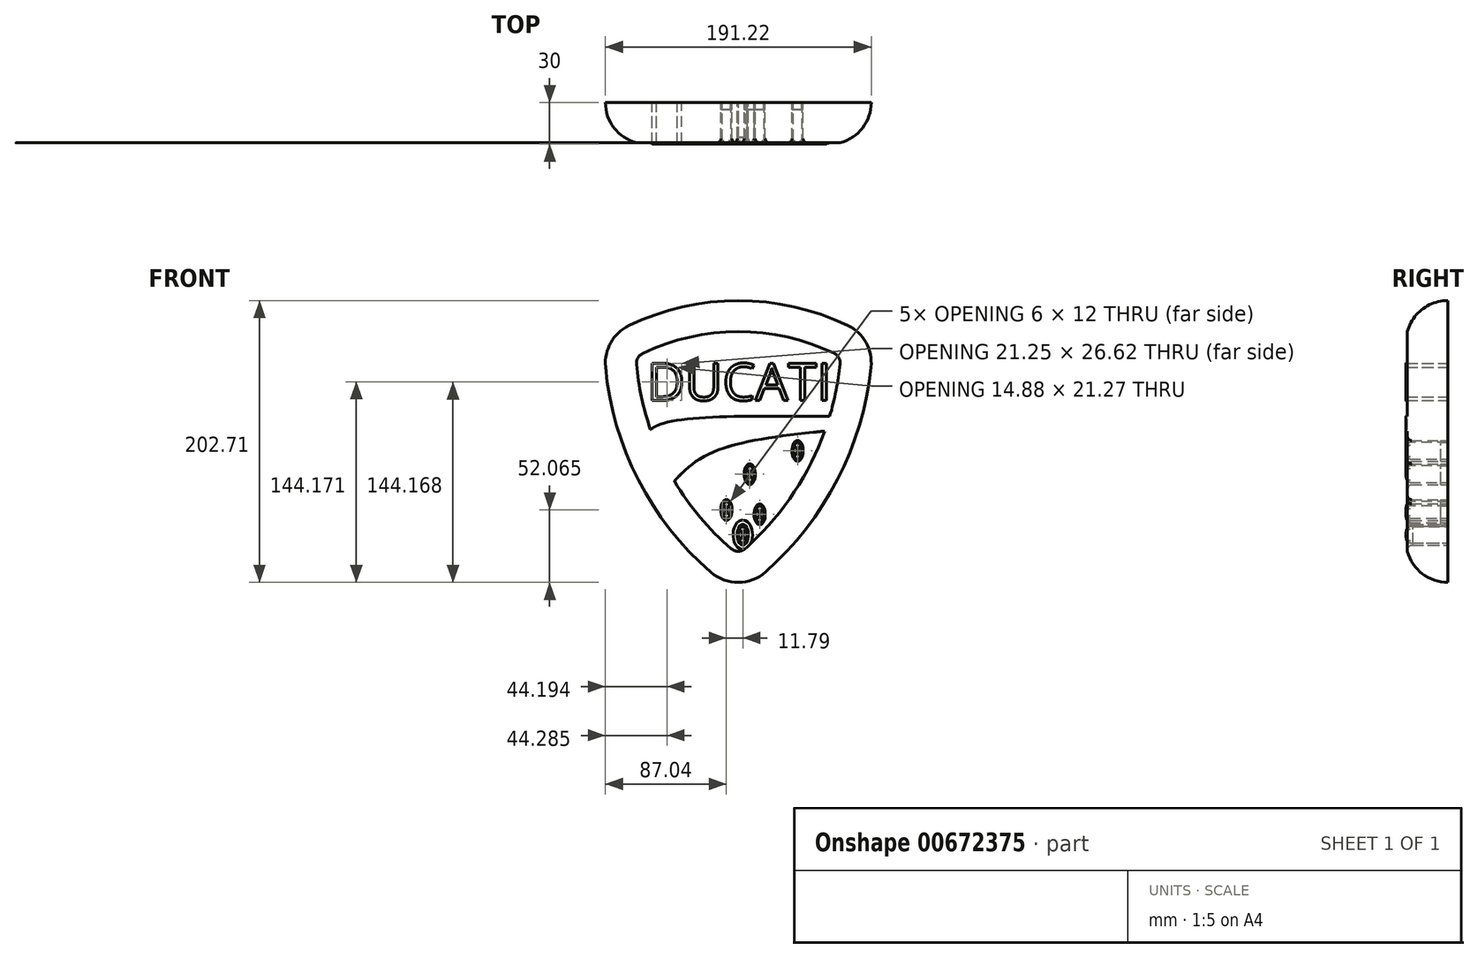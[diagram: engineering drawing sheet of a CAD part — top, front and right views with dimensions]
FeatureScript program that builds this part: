
annotation { "Feature Type Name" : "Feature", "Feature Type Description" : "" }
export const myFeature = defineFeature(function(context is Context, id is Id, definition is map)
    precondition{}
    {
        {
            var Q0;
            Q0=qCreatedBy(makeId("Front.planeOp"),FACE);
            var sketch = newSketch(context, id + "F0", { "sketchPlane" : qUnion([Q0])});
            skPoint(sketch, "E0.middle", {"position": v(0, 0) * mm});
            skArc(sketch, "E1", {"start": v(75.34, 85.7) * mm, "mid": v(-3.27, 103.48) * mm, "end": v(-81.84, 85.51) * mm});
            skArc(sketch, "E2", {"start": v(16.55, -91.67) * mm, "mid": v(68.15, -25.17) * mm, "end": v(92.22, 55.48) * mm});
            skArc(sketch, "E3", {"start": v(-98.71, 55.8) * mm, "mid": v(-75.23, -25.43) * mm, "end": v(-22.98, -91.93) * mm});
            skArc(sketch, "E4.filletArc", {"start": v(92.22, 55.48) * mm, "mid": v(88.57, 73.27) * mm, "end": v(75.34, 85.7) * mm});
            skArc(sketch, "E5.filletArc", {"start": v(-81.84, 85.51) * mm, "mid": v(-94.92, 73.3) * mm, "end": v(-98.71, 55.8) * mm});
            skArc(sketch, "E6.filletArc", {"start": v(-22.98, -91.93) * mm, "mid": v(-3.17, -99.23) * mm, "end": v(16.55, -91.67) * mm});
            skPoint(sketch, "E7", {"position": v(-75.34, 72) * mm});
            skPoint(sketch, "E8", {"position": v(-83.77, 57.14) * mm});
            skPoint(sketch, "E9", {"position": v(-3.06, 88.48) * mm});
            skPoint(sketch, "E10", {"position": v(68.86, 72.16) * mm});
            skPoint(sketch, "E11", {"position": v(77.3, 57.06) * mm});
            skPoint(sketch, "E12", {"position": v(6.6, -80.45) * mm});
            skPoint(sketch, "E13", {"position": v(-13.17, -80.58) * mm});
            skPoint(sketch, "E14", {"position": v(-75.23, -25.43) * mm});
            skPoint(sketch, "E15", {"position": v(68.15, -25.17) * mm});
            skPoint(sketch, "E16", {"position": v(55.35, -17.35) * mm});
            skArc(sketch, "E17", {"start": v(68.86, 72.16) * mm, "mid": v(-3.26, 88.48) * mm, "end": v(-75.34, 72) * mm});
            skArc(sketch, "E18", {"start": v(6.6, -80.45) * mm, "mid": v(42.72, -38.97) * mm, "end": v(67.05, 10.37) * mm});
            skArc(sketch, "E19", {"start": v(-50.14, -38.7) * mm, "mid": v(-33.09, -60.9) * mm, "end": v(-13.17, -80.58) * mm});
            skArc(sketch, "E20", {"start": v(-75.34, 72) * mm, "mid": v(-81.7, 65.79) * mm, "end": v(-83.77, 57.14) * mm});
            skArc(sketch, "E21", {"start": v(77.3, 57.06) * mm, "mid": v(75.3, 65.85) * mm, "end": v(68.86, 72.16) * mm});
            skArc(sketch, "E22", {"start": v(-13.17, -80.58) * mm, "mid": v(-3.27, -83.93) * mm, "end": v(6.6, -80.45) * mm});
            skPoint(sketch, "E23", {"position": v(-71, 62.98) * mm});
            skPoint(sketch, "E24", {"position": v(64.55, 63.14) * mm});
            skLineSegment(sketch, "E25", {"start": v(-68.8, 31.48) * mm, "end": v(62.42, 31.63) * mm, "construction": true});
            skText(sketch, "E26", { "text": "DUCATI", "fontName": "OpenSans-Regular.ttf"});
            skPoint(sketch, "E27", {"position": v(70.13, 20.17) * mm});
            skPoint(sketch, "E28", {"position": v(-71.8, 3.86) * mm});
            skPoint(sketch, "E29", {"position": v(65.47, 5.91) * mm});
            skFitSpline(sketch, "E30", {"points": [v(-71.8, 3.86) * mm, v(-60.64, 13.97) * mm, v(70.13, 20.17) * mm], "startDerivative": vector(27.5, 43.67) * mm, "endDerivative": vector(224.9, 0.03) * mm});
            skFitSpline(sketch, "E31", {"points": [v(-54.27, -32.24) * mm, v(-24.16, -6.71) * mm, v(67.05, 10.37) * mm], "startDerivative": vector(61.57, 71.85) * mm, "endDerivative": vector(173.13, 17.23) * mm});
            skArc(sketch, "E32.filletArc", {"start": v(-49.27, -26.5) * mm, "mid": v(-51.8, -32.45) * mm, "end": v(-50.14, -38.7) * mm});
            skArc(sketch, "E33", {"start": v(-83.77, 57.14) * mm, "mid": v(-79.56, 30.1) * mm, "end": v(-71.8, 3.86) * mm});
            skEllipse(sketch, "E34", {"center": v(-11.79, -47.16) * mm, "majorRadius": 7.5 * mm, "minorRadius": 4 * mm, "majorAxis": v(0, -1)});
            skEllipse(sketch, "E35", {"center": v(4.98, -21.44) * mm, "majorRadius": 7.5 * mm, "minorRadius": 4 * mm, "majorAxis": v(0, -1)});
            skEllipse(sketch, "E36", {"center": v(12.14, -50.3) * mm, "majorRadius": 7.5 * mm, "minorRadius": 4 * mm, "majorAxis": v(0, -1)});
            skEllipse(sketch, "E37", {"center": v(39.41, -4.67) * mm, "majorRadius": 7.5 * mm, "minorRadius": 4 * mm, "majorAxis": v(0, -1)});
            skPoint(sketch, "E38.start.orphan", {"position": v(-3.07, 103.48) * mm});
            skArc(sketch, "E39.trimOffspring", {"start": v(70.13, 20.17) * mm, "mid": v(74.53, 38.46) * mm, "end": v(77.3, 57.06) * mm});
            skEllipse(sketch, "E40", {"center": v(0, -65.02) * mm, "majorRadius": 7.5 * mm, "minorRadius": 4 * mm, "majorAxis": v(0, -1)});
            skEllipse(sketch, "E41", {"center": v(4.98, -21.44) * mm, "majorRadius": 6 * mm, "minorRadius": 3 * mm, "majorAxis": v(0, -1)});
            skEllipse(sketch, "E42", {"center": v(-11.79, -47.16) * mm, "majorRadius": 6 * mm, "minorRadius": 3 * mm, "majorAxis": v(0, -1)});
            skEllipse(sketch, "E43", {"center": v(0, -65.02) * mm, "majorRadius": 6 * mm, "minorRadius": 3 * mm, "majorAxis": v(0, -1)});
            skEllipse(sketch, "E44", {"center": v(12.14, -50.3) * mm, "majorRadius": 6 * mm, "minorRadius": 3 * mm, "majorAxis": v(0, -1)});
            skEllipse(sketch, "E45", {"center": v(39.41, -4.67) * mm, "majorRadius": 6 * mm, "minorRadius": 3 * mm, "majorAxis": v(0, -1)});
            const initialGuessF0  = {"E26": [-0.06883, 0.03163, 1, 0, 0.02685]};
            skSetInitialGuess(sketch, initialGuessF0);
            skSolve(sketch);
        }
        {
            var Q0;
            Q0=makeQuery(id+"F0.imprint","IMPRINT",FACE,{"disambiguationData":[TD([[makeQuery(id+"F0.imprint","IMPRINT",EDGE,{"derivedFrom":sQuery(id+"F0.wireOp",EDGE,"E1")}),1.0]])]});
            extrude(context, id + "F1", {"entities" : qUnion([Q0]), "depth" : 30 * mm, "offsetDistance" : 25 * mm});
        }
        {
            var Q0;
            Q0=makeQuery(id+"F0.imprint","IMPRINT",FACE,{"disambiguationData":[TD([[makeQuery(id+"F0.imprint","IMPRINT",EDGE,{"derivedFrom":sQuery(id+"F0.wireOp",EDGE,"E17")}),1.0]])]});
            extrude(context, id + "F2", {"entities" : qUnion([Q0]), "operationType" : NewBodyOperationType.ADD, "depth" : 29 * mm, "offsetDistance" : 25 * mm});
        }
        {
            var Q0;
            Q0=makeQuery(id+"F0.imprint","IMPRINT",FACE,{"disambiguationData":[TD([[makeQuery(id+"F0.imprint","IMPRINT",EDGE,{"derivedFrom":sQuery(id+"F0.wireOp",EDGE,"E26.sketch_text.stroke-7")}),1.0]])]});
            extrude(context, id + "F3", {"entities" : qUnion([Q0]), "depth" : 29 * mm, "offsetDistance" : 25 * mm});
        }
        {
            var Q0;
            Q0=makeQuery(id+"F0.imprint","IMPRINT",FACE,{"disambiguationData":[TD([[makeQuery(id+"F0.imprint","IMPRINT",EDGE,{"derivedFrom":sQuery(id+"F0.wireOp",EDGE,"E18")}),1.0]])]});
            extrude(context, id + "F4", {"entities" : qUnion([Q0]), "operationType" : NewBodyOperationType.ADD, "depth" : 29 * mm, "offsetDistance" : 25 * mm});
        }
        {
            var Q0;
            Q0=makeQuery(id+"F1.opExtrude","CAP_EDGE",EDGE,{"disambiguationData":[OSD([sQuery(id+"F0.wireOp",EDGE,"E3")])],"isStart":false});
            fillet(context, id + "F5", {"entities" : qUnion([Q0]), "radius" : 30 * mm, "tangentPropagation" : true, "allowEdgeOverflow" : false});
        }
        {
            var Q0;
            Q0=makeQuery(id+"F0.imprint","IMPRINT",FACE,{"disambiguationData":[TD([[makeQuery(id+"F0.imprint","IMPRINT",EDGE,{"derivedFrom":sQuery(id+"F0.wireOp",EDGE,"E41")}),1.0]])]});
            extrude(context, id + "F6", {"entities" : qUnion([Q0]), "depth" : 30 * mm, "offsetDistance" : 25 * mm});
        }
        {
            var Q0;
            Q0=makeQuery(id+"F0.imprint","IMPRINT",FACE,{"disambiguationData":[TD([[makeQuery(id+"F0.imprint","IMPRINT",EDGE,{"derivedFrom":sQuery(id+"F0.wireOp",EDGE,"E35")}),1.0]])]});
            extrude(context, id + "F7", {"entities" : qUnion([Q0]), "depth" : 5 * mm, "offsetDistance" : 25 * mm});
        }
        {
            var Q0;
            Q0=makeQuery(id+"F6.opExtrude","CAP_EDGE",EDGE,{"disambiguationData":[OSD([sQuery(id+"F0.wireOp",EDGE,"E41")])],"isStart":false});
            fillet(context, id + "F8", {"entities" : qUnion([Q0]), "radius" : 3 * mm, "tangentPropagation" : true, "allowEdgeOverflow" : false});
        }
        {
            var Q0;
            Q0=makeQuery(id+"F4.opExtrude","CAP_EDGE",EDGE,{"disambiguationData":[OSD([sQuery(id+"F0.wireOp",EDGE,"E35")])],"isStart":false});
            fillet(context, id + "F9", {"entities" : qUnion([Q0]), "radius" : 3 * mm, "tangentPropagation" : true, "allowEdgeOverflow" : false});
        }
        {
            var Q0;
            Q0=makeQuery(id+"F0.imprint","IMPRINT",FACE,{"disambiguationData":[TD([[makeQuery(id+"F0.imprint","IMPRINT",EDGE,{"derivedFrom":sQuery(id+"F0.wireOp",EDGE,"E42")}),1.0]])]});
            extrude(context, id + "F10", {"entities" : qUnion([Q0]), "depth" : 30 * mm, "offsetDistance" : 25 * mm});
        }
        {
            var Q0;
            Q0=makeQuery(id+"F0.imprint","IMPRINT",FACE,{"disambiguationData":[TD([[makeQuery(id+"F0.imprint","IMPRINT",EDGE,{"derivedFrom":sQuery(id+"F0.wireOp",EDGE,"E43")}),1.0]])]});
            extrude(context, id + "F11", {"entities" : qUnion([Q0]), "depth" : 30 * mm, "offsetDistance" : 25 * mm});
        }
        {
            var Q0;
            Q0=makeQuery(id+"F0.imprint","IMPRINT",FACE,{"disambiguationData":[TD([[makeQuery(id+"F0.imprint","IMPRINT",EDGE,{"derivedFrom":sQuery(id+"F0.wireOp",EDGE,"E44")}),1.0]])]});
            extrude(context, id + "F12", {"entities" : qUnion([Q0]), "depth" : 30 * mm, "offsetDistance" : 25 * mm});
        }
        {
            var Q0;
            Q0=makeQuery(id+"F0.imprint","IMPRINT",FACE,{"disambiguationData":[TD([[makeQuery(id+"F0.imprint","IMPRINT",EDGE,{"derivedFrom":sQuery(id+"F0.wireOp",EDGE,"E45")}),1.0]])]});
            extrude(context, id + "F13", {"entities" : qUnion([Q0]), "depth" : 30 * mm, "offsetDistance" : 25 * mm});
        }
        {
            var Q0;
            Q0=makeQuery(id+"F0.imprint","IMPRINT",FACE,{"disambiguationData":[TD([[makeQuery(id+"F0.imprint","IMPRINT",EDGE,{"derivedFrom":sQuery(id+"F0.wireOp",EDGE,"E37")}),1.0]])]});
            extrude(context, id + "F14", {"entities" : qUnion([Q0]), "depth" : 5 * mm, "offsetDistance" : 25 * mm});
        }
        {
            var Q0;
            Q0=makeQuery(id+"F13.opExtrude","CAP_EDGE",EDGE,{"disambiguationData":[OSD([sQuery(id+"F0.wireOp",EDGE,"E45")])],"isStart":false});
            var Q1;
            Q1=makeQuery(id+"F4.opExtrude","CAP_EDGE",EDGE,{"disambiguationData":[OSD([sQuery(id+"F0.wireOp",EDGE,"E37")])],"isStart":false});
            fillet(context, id + "F15", {"entities" : qUnion([Q0, Q1]), "radius" : 3 * mm, "tangentPropagation" : true, "allowEdgeOverflow" : false});
        }
        {
            var Q0;
            Q0=makeQuery(id+"F0.imprint","IMPRINT",FACE,{"disambiguationData":[TD([[makeQuery(id+"F0.imprint","IMPRINT",EDGE,{"derivedFrom":sQuery(id+"F0.wireOp",EDGE,"E34")}),1.0]])]});
            extrude(context, id + "F16", {"entities" : qUnion([Q0]), "depth" : 5 * mm, "offsetDistance" : 25 * mm});
        }
        {
            var Q0;
            Q0=makeQuery(id+"F10.opExtrude","CAP_EDGE",EDGE,{"disambiguationData":[OSD([sQuery(id+"F0.wireOp",EDGE,"E42")])],"isStart":false});
            var Q1;
            Q1=makeQuery(id+"F4.opExtrude","CAP_EDGE",EDGE,{"disambiguationData":[OSD([sQuery(id+"F0.wireOp",EDGE,"E34")])],"isStart":false});
            fillet(context, id + "F17", {"entities" : qUnion([Q0, Q1]), "radius" : 3 * mm, "tangentPropagation" : true, "allowEdgeOverflow" : false});
        }
        {
            var Q0;
            Q0=makeQuery(id+"F0.imprint","IMPRINT",FACE,{"disambiguationData":[TD([[makeQuery(id+"F0.imprint","IMPRINT",EDGE,{"derivedFrom":sQuery(id+"F0.wireOp",EDGE,"E40")}),1.0]])]});
            extrude(context, id + "F18", {"entities" : qUnion([Q0]), "depth" : 25 * mm, "offsetDistance" : 25 * mm});
        }
        {
            var Q0;
            Q0=makeQuery(id+"F11.opExtrude","CAP_EDGE",EDGE,{"disambiguationData":[OSD([sQuery(id+"F0.wireOp",EDGE,"E43")])],"isStart":false});
            var Q1;
            Q1=makeQuery(id+"F4.opExtrude","CAP_EDGE",EDGE,{"disambiguationData":[OSD([sQuery(id+"F0.wireOp",EDGE,"E40")])],"isStart":false});
            fillet(context, id + "F19", {"entities" : qUnion([Q0, Q1]), "radius" : 3 * mm, "tangentPropagation" : true, "allowEdgeOverflow" : false});
        }
        {
            var Q0;
            Q0=makeQuery(id+"F0.imprint","IMPRINT",FACE,{"disambiguationData":[TD([[makeQuery(id+"F0.imprint","IMPRINT",EDGE,{"derivedFrom":sQuery(id+"F0.wireOp",EDGE,"E36")}),1.0]])]});
            extrude(context, id + "F20", {"entities" : qUnion([Q0]), "depth" : 5 * mm, "offsetDistance" : 25 * mm});
        }
        {
            var Q0;
            Q0=makeQuery(id+"F12.opExtrude","CAP_EDGE",EDGE,{"disambiguationData":[OSD([sQuery(id+"F0.wireOp",EDGE,"E44")])],"isStart":false});
            var Q1;
            Q1=makeQuery(id+"F4.opExtrude","CAP_EDGE",EDGE,{"disambiguationData":[OSD([sQuery(id+"F0.wireOp",EDGE,"E36")])],"isStart":false});
            fillet(context, id + "F21", {"entities" : qUnion([Q0, Q1]), "radius" : 3 * mm, "tangentPropagation" : true, "allowEdgeOverflow" : false});
        }
        {
            var Q0;
            Q0=makeQuery(id+"F0.imprint","IMPRINT",FACE,{"disambiguationData":[TD([[makeQuery(id+"F0.imprint","IMPRINT",EDGE,{"derivedFrom":sQuery(id+"F0.wireOp",EDGE,"E26.sketch_text.stroke-0")}),-1.0]])]});
            extrude(context, id + "F22", {"entities" : qUnion([Q0]), "depth" : 30 * mm, "offsetDistance" : 25 * mm});
        }
        {
            var Q0;
            Q0=makeQuery(id+"F0.imprint","IMPRINT",FACE,{"disambiguationData":[TD([[makeQuery(id+"F0.imprint","IMPRINT",EDGE,{"derivedFrom":sQuery(id+"F0.wireOp",EDGE,"E26.sketch_text.stroke-14")}),-1.0]])]});
            extrude(context, id + "F23", {"entities" : qUnion([Q0]), "operationType" : NewBodyOperationType.ADD, "depth" : 30 * mm, "offsetDistance" : 25 * mm});
        }
        {
            var Q0;
            Q0=makeQuery(id+"F0.imprint","IMPRINT",FACE,{"disambiguationData":[TD([[makeQuery(id+"F0.imprint","IMPRINT",EDGE,{"derivedFrom":sQuery(id+"F0.wireOp",EDGE,"E26.sketch_text.stroke-28")}),-1.0]])]});
            extrude(context, id + "F24", {"entities" : qUnion([Q0]), "operationType" : NewBodyOperationType.ADD, "depth" : 30 * mm, "offsetDistance" : 25 * mm});
        }
        {
            var Q0;
            Q0=makeQuery(id+"F0.imprint","IMPRINT",FACE,{"disambiguationData":[TD([[makeQuery(id+"F0.imprint","IMPRINT",EDGE,{"derivedFrom":sQuery(id+"F0.wireOp",EDGE,"E26.sketch_text.stroke-43")}),-1.0]])]});
            extrude(context, id + "F25", {"entities" : qUnion([Q0]), "operationType" : NewBodyOperationType.ADD, "depth" : 30 * mm, "offsetDistance" : 25 * mm});
        }
        {
            var Q0;
            Q0=makeQuery(id+"F0.imprint","IMPRINT",FACE,{"disambiguationData":[TD([[makeQuery(id+"F0.imprint","IMPRINT",EDGE,{"derivedFrom":sQuery(id+"F0.wireOp",EDGE,"E26.sketch_text.stroke-51")}),1.0]])]});
            extrude(context, id + "F26", {"entities" : qUnion([Q0]), "operationType" : NewBodyOperationType.ADD, "depth" : 29 * mm, "offsetDistance" : 25 * mm});
        }
        {
            var Q0;
            Q0=makeQuery(id+"F0.imprint","IMPRINT",FACE,{"disambiguationData":[TD([[makeQuery(id+"F0.imprint","IMPRINT",EDGE,{"derivedFrom":sQuery(id+"F0.wireOp",EDGE,"E26.sketch_text.stroke-56")}),-1.0]])]});
            extrude(context, id + "F27", {"entities" : qUnion([Q0]), "operationType" : NewBodyOperationType.ADD, "depth" : 30 * mm, "offsetDistance" : 25 * mm});
        }
        {
            var Q0;
            Q0=makeQuery(id+"F0.imprint","IMPRINT",FACE,{"disambiguationData":[TD([[makeQuery(id+"F0.imprint","IMPRINT",EDGE,{"derivedFrom":sQuery(id+"F0.wireOp",EDGE,"E26.sketch_text.stroke-64")}),-1.0]])]});
            extrude(context, id + "F28", {"entities" : qUnion([Q0]), "operationType" : NewBodyOperationType.ADD, "depth" : 30 * mm, "offsetDistance" : 25 * mm});
        }
    });
